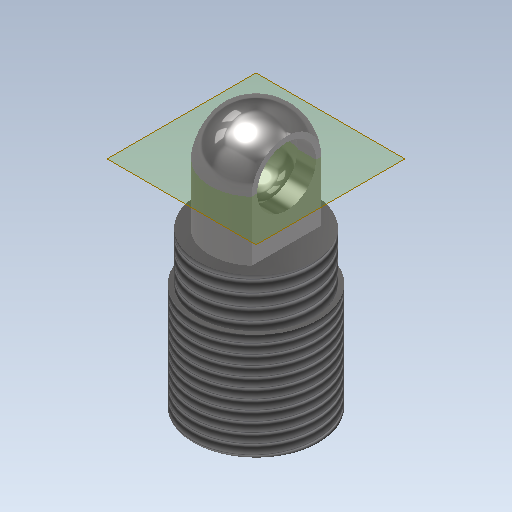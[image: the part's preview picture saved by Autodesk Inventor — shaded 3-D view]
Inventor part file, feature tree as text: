
AUTODESK INVENTOR PART (.ipt)
format: ipt  version: 2020 (Build 240168000, 168)  size: 218,624 bytes
history: native  units: mm
features: sketch x6, extrude x3, revolve x2, hole x2, thread x2, plane x1, other x1
ambient origin geometry x8: Origin, YZ Plane, XZ Plane, XY Plane, X Axis, Y Axis, Z Axis, Center Point
bodies: Solid1 (feature_tree)
feature tree (17):
  extrude  "Extrusion1"  Depth=11.0mm TaperAngle=0.0deg
  extrude  "Extrusion2"  Depth=5.0mm TaperAngle=0.0deg
  revolve  "Revolution1"  Angle=90.0deg
  extrude  "Extrusion3"  Depth=5.0mm TaperAngle=0.0deg
  hole  "Hole1"  [1 undecoded]
  thread  "Thread1"  [1 undecoded]
  thread  "Thread2"  [1 undecoded]
  hole  "Hole2"  [1 undecoded]
  plane  "Work Plane1"
  revolve  "Revolution2"  [1 undecoded]
  sketch  "Sketch1"  dims[d0=12.917mm d1=11.0mm d2=0.0mm]
  sketch  "Sketch2"  dims[d3=12.0mm d4=5.0mm d5=0.0mm]
  sketch  "Sketch3"  dims[d7=4.8mm d8=90.0deg]
  sketch  "Sketch4"  dims[d9=5.0mm d10=13.25mm d11=0.0mm]
  sketch  "Sketch5"  dims[d13=22.2mm d14=10.0mm d15=10.0mm]
  other  "Work Axis1"
  sketch  "Sketch6"  dims[d16=6.1mm d17=6.0mm d18=4.0mm d19=2.0mm d20=90.0deg d21=8.0mm d22=20.594885mm d23=10.0mm d24=0.0mm d25=10.0mm d26=0.0mm d27=12.0mm d28=10.917mm d29=8.5mm d30=4.0mm d31=2.0mm d32=90.0deg d33=10.0mm d34=0.0mm d35=0.0mm d36=6.6mm d37=90.0deg]
note: 5 required parameter values undecoded (feature->parameter linkage not recoverable at this tier; creation-order binding heuristic only, values carry confidence <= 0.55)